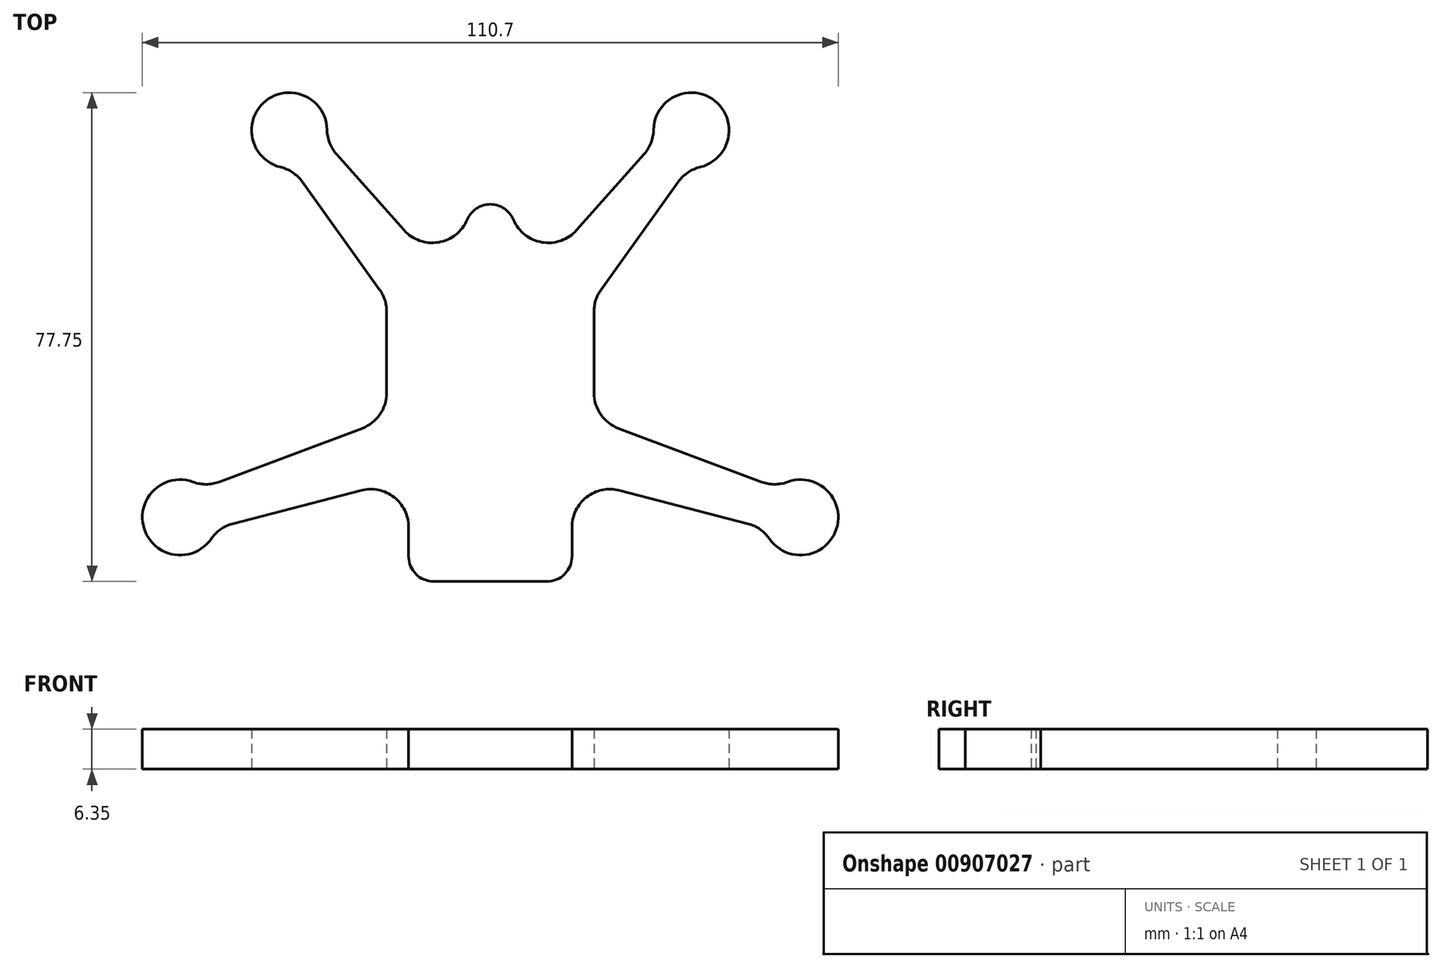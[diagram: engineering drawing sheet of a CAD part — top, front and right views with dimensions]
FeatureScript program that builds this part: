
annotation { "Feature Type Name" : "Feature", "Feature Type Description" : "" }
export const myFeature = defineFeature(function(context is Context, id is Id, definition is map)
    precondition{}
    {
        {
            var Q0;
            Q0=qCreatedBy(makeId("Top.planeOp"),FACE);
            var sketch = newSketch(context, id + "F0", { "sketchPlane" : qUnion([Q0])});
            skCircle(sketch, "E0", {"center": v(-31.98, 42.25) * mm, "radius": 30.48 * mm});
            skCircle(sketch, "E1", {"center": v(31.98, 42.25) * mm, "radius": 30.48 * mm});
            skCircle(sketch, "E2", {"center": v(-49.35, -19.3) * mm, "radius": 30.48 * mm});
            skCircle(sketch, "E3", {"center": v(49.35, -19.3) * mm, "radius": 30.48 * mm});
            skCircle(sketch, "E4", {"center": v(0, 0) * mm, "radius": 22.51 * mm});
            skLineSegment(sketch, "E5.bottom", {"start": v(-13.5, 13.5) * mm, "end": v(13.5, 13.5) * mm});
            skLineSegment(sketch, "E5.top", {"start": v(-13.5, -13.5) * mm, "end": v(13.5, -13.5) * mm});
            skLineSegment(sketch, "E5.left", {"start": v(-13.5, 13.5) * mm, "end": v(-13.5, -13.5) * mm});
            skLineSegment(sketch, "E5.right", {"start": v(13.5, 13.5) * mm, "end": v(13.5, -13.5) * mm});
            skCircle(sketch, "E6", {"center": v(-10, 10) * mm, "radius": 1.1 * mm});
            skCircle(sketch, "E7", {"center": v(-10, -10) * mm, "radius": 1.1 * mm});
            skCircle(sketch, "E8", {"center": v(10, -10) * mm, "radius": 1.1 * mm});
            skCircle(sketch, "E9", {"center": v(10, 10) * mm, "radius": 1.1 * mm});
            skLineSegment(sketch, "E10", {"start": v(-10, 10) * mm, "end": v(10, -10) * mm, "construction": true});
            skSolve(sketch);
        }
        {
            var Q0;
            Q0=qCreatedBy(makeId("Top.planeOp"),FACE);
            var sketch = newSketch(context, id + "F1", { "sketchPlane" : qUnion([Q0])});
            skLineSegment(sketch, "E11", {"start": v(43.1, -13.66) * mm, "end": v(20.4, -5.14) * mm});
            skLineSegment(sketch, "E12", {"start": v(17.63, 16.96) * mm, "end": v(29.93, 34.1) * mm});
            skLineSegment(sketch, "E13", {"start": v(24.46, 38.47) * mm, "end": v(13.7, 26.38) * mm});
            skLineSegment(sketch, "E14", {"start": v(20.5, -15.01) * mm, "end": v(41, -20.33) * mm});
            skArc(sketch, "E15", {"start": v(33.4, 36.42) * mm, "mid": v(35.73, 46.94) * mm, "end": v(25.98, 42.35) * mm});
            skLineSegment(sketch, "E16", {"start": v(0, 30.5) * mm, "end": v(0, -29.5) * mm});
            skPoint(sketch, "E17.end.orphan", {"position": v(-27.37, 48) * mm});
            skPoint(sketch, "E18.start.orphan", {"position": v(-35.88, 44.15) * mm});
            skLineSegment(sketch, "E19", {"start": v(16.5, 13.46) * mm, "end": v(16.5, 0.48) * mm});
            skArc(sketch, "E20", {"start": v(44.42, -22.72) * mm, "mid": v(55.07, -21.11) * mm, "end": v(47.28, -13.67) * mm});
            skLineSegment(sketch, "E21", {"start": v(0, -3.7) * mm, "end": v(49.35, -19.3) * mm, "construction": true});
            skCircle(sketch, "E22", {"center": v(10, -10) * mm, "radius": 3 * mm, "construction": true});
            skCircle(sketch, "E23", {"center": v(10, 10) * mm, "radius": 3 * mm, "construction": true});
            skLineSegment(sketch, "E24", {"start": v(31.98, 42.25) * mm, "end": v(0, 2.3) * mm, "construction": true});
            skArc(sketch, "E25.filletArc", {"start": v(24.46, 38.47) * mm, "mid": v(25.57, 40.27) * mm, "end": v(25.98, 42.35) * mm});
            skArc(sketch, "E26.filletArc", {"start": v(33.4, 36.42) * mm, "mid": v(31.45, 35.57) * mm, "end": v(29.93, 34.1) * mm});
            skArc(sketch, "E27.filletArc", {"start": v(43.1, -13.66) * mm, "mid": v(45.2, -14.04) * mm, "end": v(47.28, -13.67) * mm});
            skArc(sketch, "E28.filletArc", {"start": v(44.42, -22.72) * mm, "mid": v(42.92, -21.22) * mm, "end": v(41, -20.33) * mm});
            skPoint(sketch, "E29.visualSharp", {"position": v(16.5, 15.4) * mm});
            skArc(sketch, "E29.filletArc", {"start": v(17.63, 16.96) * mm, "mid": v(16.79, 15.3) * mm, "end": v(16.5, 13.46) * mm});
            skArc(sketch, "E30.filletArc", {"start": v(16.5, 0.48) * mm, "mid": v(17.57, -2.94) * mm, "end": v(20.4, -5.14) * mm});
            skArc(sketch, "E31", {"start": v(3.69, 28.05) * mm, "mid": v(2.21, 29.83) * mm, "end": v(0, 30.5) * mm});
            skArc(sketch, "E32", {"start": v(3.69, 28.05) * mm, "mid": v(8.24, 24.45) * mm, "end": v(13.7, 26.38) * mm});
            skLineSegment(sketch, "E33", {"start": v(0, -29.5) * mm, "end": v(9, -29.5) * mm});
            skLineSegment(sketch, "E34", {"start": v(13, -25.5) * mm, "end": v(13, -20.82) * mm});
            skArc(sketch, "E35.filletArc", {"start": v(20.5, -15.01) * mm, "mid": v(15.33, -16.07) * mm, "end": v(13, -20.82) * mm});
            skArc(sketch, "E36.filletArc", {"start": v(9, -29.5) * mm, "mid": v(11.83, -28.33) * mm, "end": v(13, -25.5) * mm});
            skSolve(sketch);
        }
        {
            var Q0;
            Q0 = qSketchRegion(id + "F1", true);
            extrude(context, id + "F2", {"entities" : qUnion([Q0]), "depth" : 6.35 * mm, "offsetDistance" : 25 * mm});
        }
        {
            var Q0;
            Q0=makeQuery(id+"F2.opExtrude","SWEPT_BODY",BODY,{"disambiguationData":[OSD([sQuery(id+"F1.wireOp",EDGE,"E11"),sQuery(id+"F1.wireOp",EDGE,"E12"),sQuery(id+"F1.wireOp",EDGE,"E13"),sQuery(id+"F1.wireOp",EDGE,"E14"),sQuery(id+"F1.wireOp",EDGE,"E15"),sQuery(id+"F1.wireOp",EDGE,"E16"),sQuery(id+"F1.wireOp",EDGE,"E19"),sQuery(id+"F1.wireOp",EDGE,"E20"),sQuery(id+"F1.wireOp",EDGE,"E25.filletArc"),sQuery(id+"F1.wireOp",EDGE,"E26.filletArc"),sQuery(id+"F1.wireOp",EDGE,"E27.filletArc"),sQuery(id+"F1.wireOp",EDGE,"E28.filletArc"),sQuery(id+"F1.wireOp",EDGE,"E29.filletArc"),sQuery(id+"F1.wireOp",EDGE,"E30.filletArc"),sQuery(id+"F1.wireOp",EDGE,"E31"),sQuery(id+"F1.wireOp",EDGE,"E32"),sQuery(id+"F1.wireOp",EDGE,"E33"),sQuery(id+"F1.wireOp",EDGE,"E34"),sQuery(id+"F1.wireOp",EDGE,"E35.filletArc"),sQuery(id+"F1.wireOp",EDGE,"E36.filletArc")])]});
            var Q1;
            Q1=qCreatedBy(makeId("Right.planeOp"),FACE);
            mirror(context, id + "F3", {"operationType" : NewBodyOperationType.ADD, "entities" : qUnion([Q0]), "mirrorPlane" : qUnion([Q1])});
        }
    });
